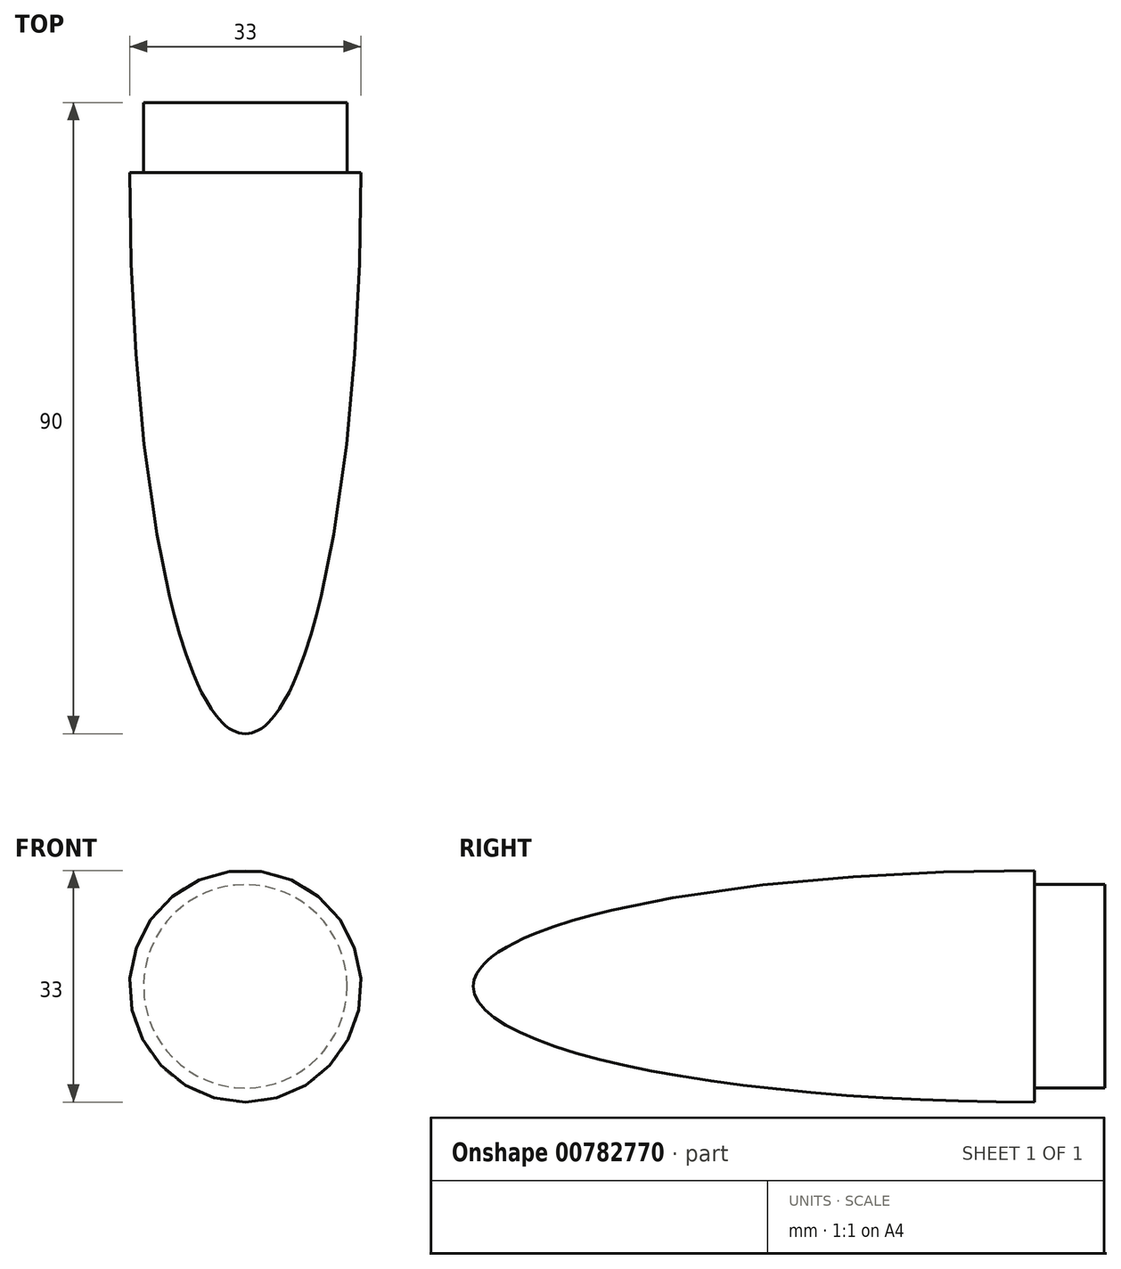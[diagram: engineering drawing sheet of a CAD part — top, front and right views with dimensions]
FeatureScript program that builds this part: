
annotation { "Feature Type Name" : "Feature", "Feature Type Description" : "" }
export const myFeature = defineFeature(function(context is Context, id is Id, definition is map)
    precondition{}
    {
        {
            var Q0;
            Q0=qCreatedBy(makeId("Right.planeOp"),FACE);
            var sketch = newSketch(context, id + "F0", { "sketchPlane" : qUnion([Q0])});
            skLineSegment(sketch, "E0.bottom", {"start": v(0, 0) * mm, "end": v(10, 0) * mm});
            skLineSegment(sketch, "E0.top", {"start": v(0, -14.5) * mm, "end": v(10, -14.5) * mm});
            skLineSegment(sketch, "E0.left", {"start": v(0, 0) * mm, "end": v(0, -14.5) * mm});
            skLineSegment(sketch, "E0.right", {"start": v(10, 0) * mm, "end": v(10, -14.5) * mm});
            skLineSegment(sketch, "E1.bottom", {"start": v(0, 0) * mm, "end": v(-80, 0) * mm});
            skLineSegment(sketch, "E1.top", {"start": v(0, -16.5) * mm, "end": v(-80, -16.5) * mm});
            skLineSegment(sketch, "E1.left", {"start": v(0, 0) * mm, "end": v(0, -16.5) * mm});
            skLineSegment(sketch, "E1.right", {"start": v(-80, 0) * mm, "end": v(-80, -16.5) * mm});
            skEllipse(sketch, "E2", {"center": v(0, 0) * mm, "majorRadius": 80 * mm, "minorRadius": 16.5 * mm, "majorAxis": v(-1, 0)});
            skSolve(sketch);
        }
        {
            var Q0;
            Q0=makeQuery(id+"F0.imprint","IMPRINT",FACE,{"disambiguationData":[TD([[makeQuery(id+"F0.imprint","IMPRINT",EDGE,{"derivedFrom":sQuery(id+"F0.wireOp",EDGE,"E0.left")}),-1.0]])]});
            var Q1;
            Q1=makeQuery(id+"F0.imprint","IMPRINT",FACE,{"disambiguationData":[TD([[makeQuery(id+"F0.imprint","IMPRINT",EDGE,{"derivedFrom":sQuery(id+"F0.wireOp",EDGE,"E0.bottom")}),-1.0]])]});
            var Q2;
            Q2=sQuery(id+"F0.wireOp",EDGE,"E1.bottom");
            revolve(context, id + "F1", {"entities" : qUnion([Q0, Q1]), "axis" : qUnion([Q2]), "revolveType" : RevolveType.FULL});
        }
    });
